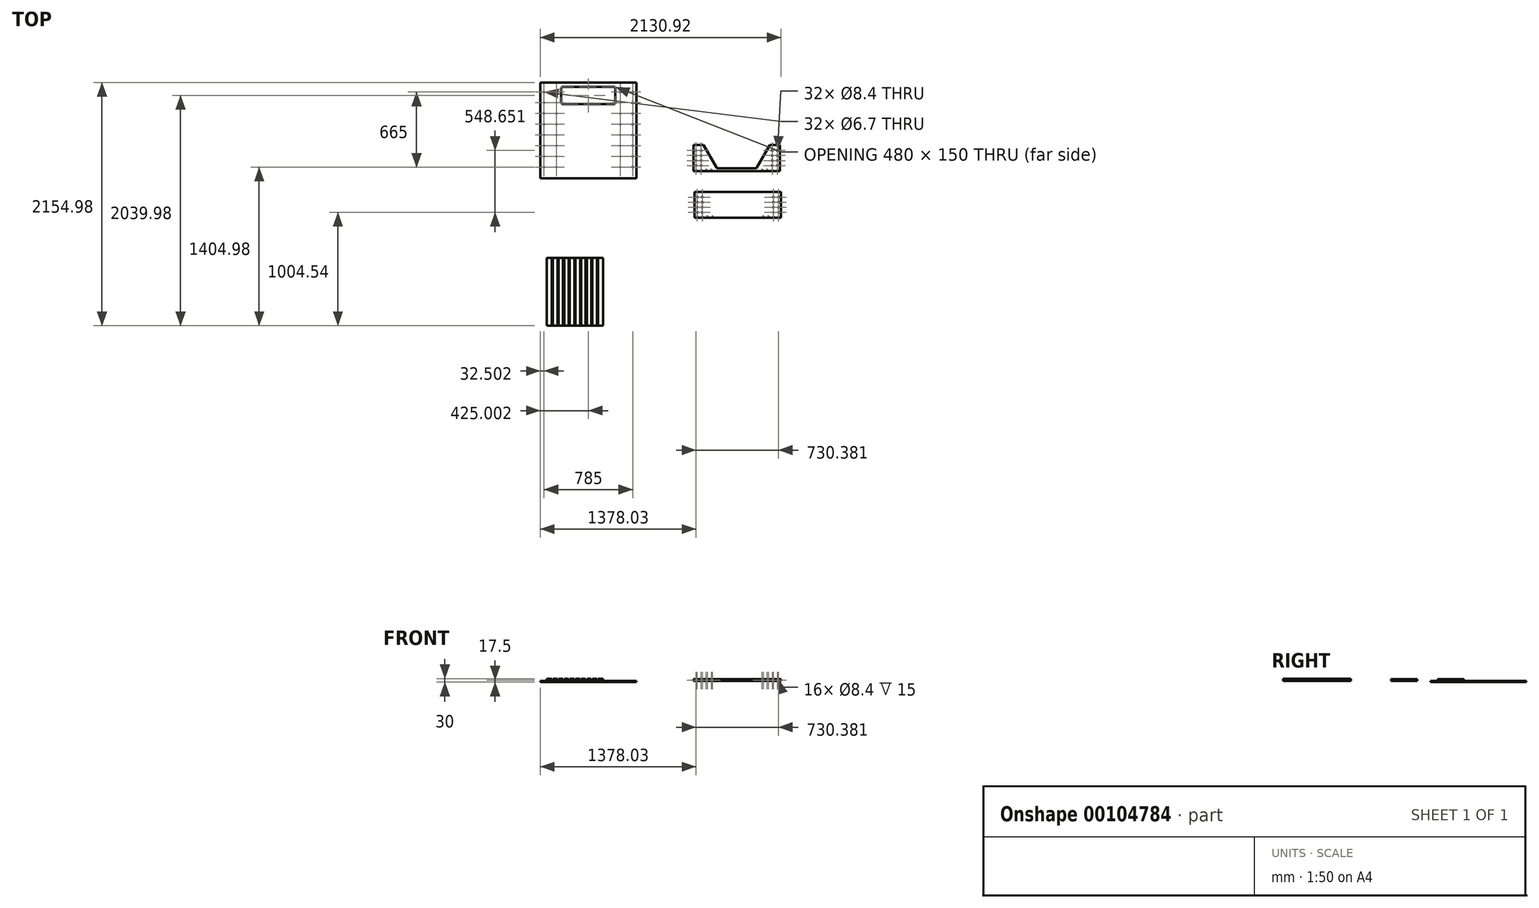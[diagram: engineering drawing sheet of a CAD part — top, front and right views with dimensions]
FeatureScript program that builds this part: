
annotation { "Feature Type Name" : "Feature", "Feature Type Description" : "" }
export const myFeature = defineFeature(function(context is Context, id is Id, definition is map)
    precondition{}
    {
        {
            var Q0;
            Q0=qCreatedBy(makeId("Top.planeOp"),FACE);
            var sketch = newSketch(context, id + "F0", { "sketchPlane" : qUnion([Q0])});
            skLineSegment(sketch, "E0", {"start": v(-189.52, -105.86) * mm, "end": v(-189.52, -335.86) * mm});
            skLineSegment(sketch, "E1", {"start": v(17.97, -309.36) * mm, "end": v(-99.52, -105.86) * mm});
            skLineSegment(sketch, "E2", {"start": v(-99.52, -105.86) * mm, "end": v(-189.52, -105.86) * mm});
            skLineSegment(sketch, "E3", {"start": v(575.48, -335.86) * mm, "end": v(575.48, -105.86) * mm});
            skLineSegment(sketch, "E4", {"start": v(575.48, -105.86) * mm, "end": v(485.48, -105.86) * mm});
            skLineSegment(sketch, "E5", {"start": v(485.48, -105.86) * mm, "end": v(368, -309.36) * mm});
            skLineSegment(sketch, "E6", {"start": v(365.4, -310.86) * mm, "end": v(20.57, -310.86) * mm});
            skLineSegment(sketch, "E7", {"start": v(-189.52, -335.86) * mm, "end": v(575.48, -335.86) * mm});
            skPoint(sketch, "E8.visualSharp", {"position": v(367.13, -310.86) * mm});
            skArc(sketch, "E8.filletArc", {"start": v(365.4, -310.86) * mm, "mid": v(366.9, -310.45) * mm, "end": v(368, -309.36) * mm});
            skPoint(sketch, "E9.visualSharp", {"position": v(18.84, -310.86) * mm});
            skArc(sketch, "E9.filletArc", {"start": v(17.97, -309.36) * mm, "mid": v(19.07, -310.45) * mm, "end": v(20.57, -310.86) * mm});
            skCircle(sketch, "E10", {"center": v(-167.02, -153.36) * mm, "radius": 4.2 * mm});
            skCircle(sketch, "E11", {"center": v(-122.02, -153.36) * mm, "radius": 4.2 * mm});
            skCircle(sketch, "E12", {"center": v(-167.02, -198.36) * mm, "radius": 4.2 * mm});
            skCircle(sketch, "E13", {"center": v(-122.02, -198.36) * mm, "radius": 4.2 * mm});
            skCircle(sketch, "E14", {"center": v(-167.02, -243.36) * mm, "radius": 4.2 * mm});
            skCircle(sketch, "E15", {"center": v(-122.02, -243.36) * mm, "radius": 4.2 * mm});
            skCircle(sketch, "E16", {"center": v(-167.02, -288.36) * mm, "radius": 4.2 * mm});
            skCircle(sketch, "E17", {"center": v(-122.02, -288.36) * mm, "radius": 4.2 * mm});
            skCircle(sketch, "E18", {"center": v(507.98, -153.36) * mm, "radius": 4.2 * mm});
            skCircle(sketch, "E19", {"center": v(552.98, -153.36) * mm, "radius": 4.2 * mm});
            skCircle(sketch, "E20", {"center": v(507.98, -198.36) * mm, "radius": 4.2 * mm});
            skCircle(sketch, "E21", {"center": v(552.98, -198.36) * mm, "radius": 4.2 * mm});
            skCircle(sketch, "E22", {"center": v(507.98, -243.36) * mm, "radius": 4.2 * mm});
            skCircle(sketch, "E23", {"center": v(552.98, -243.36) * mm, "radius": 4.2 * mm});
            skCircle(sketch, "E24", {"center": v(507.98, -288.36) * mm, "radius": 4.2 * mm});
            skCircle(sketch, "E25", {"center": v(552.98, -288.36) * mm, "radius": 4.2 * mm});
            skLineSegment(sketch, "E26.bottom", {"start": v(-179.13, -519.5) * mm, "end": v(585.87, -519.5) * mm});
            skLineSegment(sketch, "E26.top", {"start": v(-179.13, -749.5) * mm, "end": v(585.87, -749.5) * mm});
            skLineSegment(sketch, "E26.left", {"start": v(-179.13, -519.5) * mm, "end": v(-179.13, -749.5) * mm});
            skLineSegment(sketch, "E26.right", {"start": v(585.87, -519.5) * mm, "end": v(585.87, -749.5) * mm});
            skCircle(sketch, "E27", {"center": v(-156.63, -567) * mm, "radius": 4.2 * mm});
            skCircle(sketch, "E28", {"center": v(-111.63, -567) * mm, "radius": 4.2 * mm});
            skCircle(sketch, "E29", {"center": v(-156.63, -612) * mm, "radius": 4.2 * mm});
            skCircle(sketch, "E30", {"center": v(-111.63, -612) * mm, "radius": 4.2 * mm});
            skCircle(sketch, "E31", {"center": v(-156.63, -657) * mm, "radius": 4.2 * mm});
            skCircle(sketch, "E32", {"center": v(-111.63, -657) * mm, "radius": 4.2 * mm});
            skCircle(sketch, "E33", {"center": v(-156.63, -702) * mm, "radius": 4.2 * mm});
            skCircle(sketch, "E34", {"center": v(-111.63, -702) * mm, "radius": 4.2 * mm});
            skCircle(sketch, "E35", {"center": v(518.37, -567) * mm, "radius": 4.2 * mm});
            skCircle(sketch, "E36", {"center": v(563.37, -567) * mm, "radius": 4.2 * mm});
            skCircle(sketch, "E37", {"center": v(518.37, -612) * mm, "radius": 4.2 * mm});
            skCircle(sketch, "E38", {"center": v(563.37, -612) * mm, "radius": 4.2 * mm});
            skCircle(sketch, "E39", {"center": v(518.37, -657) * mm, "radius": 4.2 * mm});
            skCircle(sketch, "E40", {"center": v(563.37, -657) * mm, "radius": 4.2 * mm});
            skCircle(sketch, "E41", {"center": v(518.37, -702) * mm, "radius": 4.2 * mm});
            skCircle(sketch, "E42", {"center": v(563.37, -702) * mm, "radius": 4.2 * mm});
            skLineSegment(sketch, "E43.bottom", {"start": v(-1545.05, 448.43) * mm, "end": v(-695.05, 448.43) * mm});
            skLineSegment(sketch, "E43.top", {"start": v(-1545.05, -401.57) * mm, "end": v(-695.05, -401.57) * mm});
            skLineSegment(sketch, "E43.left", {"start": v(-1545.05, 448.43) * mm, "end": v(-1545.05, -401.57) * mm});
            skLineSegment(sketch, "E43.right", {"start": v(-695.05, 448.43) * mm, "end": v(-695.05, -401.57) * mm});
            skPoint(sketch, "E44", {"position": v(-1512.55, 363.43) * mm});
            skPoint(sketch, "E45", {"position": v(-1402.55, 363.43) * mm});
            skPoint(sketch, "E46", {"position": v(-837.55, 363.43) * mm});
            skPoint(sketch, "E47", {"position": v(-727.55, 363.43) * mm});
            skPoint(sketch, "E48", {"position": v(-1512.55, -301.57) * mm});
            skPoint(sketch, "E49", {"position": v(-1402.55, -301.57) * mm});
            skPoint(sketch, "E50", {"position": v(-837.55, -301.57) * mm});
            skPoint(sketch, "E51", {"position": v(-727.55, -301.57) * mm});
            skPoint(sketch, "E52", {"position": v(-1512.55, 268.43) * mm});
            skPoint(sketch, "E53", {"position": v(-1512.55, -16.57) * mm});
            skPoint(sketch, "E54", {"position": v(-1512.55, -206.57) * mm});
            skPoint(sketch, "E55", {"position": v(-1512.55, -111.57) * mm});
            skPoint(sketch, "E56", {"position": v(-1512.55, 78.43) * mm});
            skPoint(sketch, "E57", {"position": v(-1512.55, 173.43) * mm});
            skPoint(sketch, "E58", {"position": v(-1402.55, 268.43) * mm});
            skPoint(sketch, "E59", {"position": v(-1402.55, 173.43) * mm});
            skPoint(sketch, "E60", {"position": v(-1402.55, 78.43) * mm});
            skPoint(sketch, "E61", {"position": v(-1402.55, -16.57) * mm});
            skPoint(sketch, "E62", {"position": v(-1402.55, -111.57) * mm});
            skPoint(sketch, "E63", {"position": v(-1402.55, -206.57) * mm});
            skPoint(sketch, "E64", {"position": v(-837.55, 268.43) * mm});
            skPoint(sketch, "E65", {"position": v(-837.55, 173.43) * mm});
            skPoint(sketch, "E66", {"position": v(-837.55, 78.43) * mm});
            skPoint(sketch, "E67", {"position": v(-837.55, -16.57) * mm});
            skPoint(sketch, "E68", {"position": v(-837.55, -111.57) * mm});
            skPoint(sketch, "E69", {"position": v(-837.55, -206.57) * mm});
            skPoint(sketch, "E70", {"position": v(-727.55, 268.43) * mm});
            skPoint(sketch, "E71", {"position": v(-727.55, 173.43) * mm});
            skPoint(sketch, "E72", {"position": v(-727.55, 78.43) * mm});
            skPoint(sketch, "E73", {"position": v(-727.55, -16.57) * mm});
            skPoint(sketch, "E74", {"position": v(-727.55, -111.57) * mm});
            skPoint(sketch, "E75", {"position": v(-727.55, -206.57) * mm});
            skLineSegment(sketch, "E76.bottom", {"start": v(-1488.78, -1106.55) * mm, "end": v(-988.78, -1106.55) * mm});
            skLineSegment(sketch, "E76.top", {"start": v(-1488.78, -1706.55) * mm, "end": v(-988.78, -1706.55) * mm});
            skLineSegment(sketch, "E76.left", {"start": v(-1488.78, -1106.55) * mm, "end": v(-1488.78, -1706.55) * mm});
            skLineSegment(sketch, "E76.right", {"start": v(-988.78, -1106.55) * mm, "end": v(-988.78, -1706.55) * mm});
            skLineSegment(sketch, "E77.bottom", {"start": v(-1350.05, 408.43) * mm, "end": v(-890.05, 408.43) * mm});
            skLineSegment(sketch, "E77.top", {"start": v(-1350.05, 258.43) * mm, "end": v(-890.05, 258.43) * mm});
            skLineSegment(sketch, "E77.left", {"start": v(-1360.05, 398.43) * mm, "end": v(-1360.05, 268.43) * mm});
            skLineSegment(sketch, "E77.right", {"start": v(-880.05, 398.43) * mm, "end": v(-880.05, 268.43) * mm});
            skPoint(sketch, "E78.visualSharp", {"position": v(-1360.05, 408.43) * mm});
            skArc(sketch, "E78.filletArc", {"start": v(-1350.05, 408.43) * mm, "mid": v(-1357.12, 405.5) * mm, "end": v(-1360.05, 398.43) * mm});
            skPoint(sketch, "E79.visualSharp", {"position": v(-1360.05, 258.43) * mm});
            skArc(sketch, "E79.filletArc", {"start": v(-1360.05, 268.43) * mm, "mid": v(-1357.12, 261.36) * mm, "end": v(-1350.05, 258.43) * mm});
            skPoint(sketch, "E80.visualSharp", {"position": v(-880.05, 408.43) * mm});
            skArc(sketch, "E80.filletArc", {"start": v(-880.05, 398.43) * mm, "mid": v(-882.98, 405.5) * mm, "end": v(-890.05, 408.43) * mm});
            skPoint(sketch, "E81.visualSharp", {"position": v(-880.05, 258.43) * mm});
            skArc(sketch, "E81.filletArc", {"start": v(-890.05, 258.43) * mm, "mid": v(-882.98, 261.36) * mm, "end": v(-880.05, 268.43) * mm});
            skSolve(sketch);
        }
        {
            var Q0;
            Q0=makeQuery(id+"F0.imprint","IMPRINT",FACE,{"disambiguationData":[TD([[makeQuery(id+"F0.imprint","IMPRINT",EDGE,{"derivedFrom":sQuery(id+"F0.wireOp",EDGE,"E0")}),1.0]])]});
            extrude(context, id + "F1", {"entities" : qUnion([Q0]), "depth" : 15 * mm});
        }
        {
            var Q0;
            Q0=makeQuery(id+"F1.opExtrude","SWEPT_FACE",FACE,{"disambiguationData":[OSD([sQuery(id+"F0.wireOp",EDGE,"E7")])]});
            var sketch = newSketch(context, id + "F2", { "sketchPlane" : qUnion([Q0])});
            skCircle(sketch, "E82", {"center": v(-167.02, 7.5) * mm, "radius": 4.2 * mm});
            skCircle(sketch, "E83", {"center": v(-122.02, 7.5) * mm, "radius": 4.2 * mm});
            skCircle(sketch, "E84", {"center": v(-77.02, 7.5) * mm, "radius": 4.2 * mm});
            skCircle(sketch, "E85", {"center": v(-32.02, 7.5) * mm, "radius": 4.2 * mm});
            skCircle(sketch, "E86", {"center": v(552.98, 7.5) * mm, "radius": 4.2 * mm});
            skCircle(sketch, "E87", {"center": v(507.98, 7.5) * mm, "radius": 4.2 * mm});
            skCircle(sketch, "E88", {"center": v(462.98, 7.5) * mm, "radius": 4.2 * mm});
            skCircle(sketch, "E89", {"center": v(417.98, 7.5) * mm, "radius": 4.2 * mm});
            skPoint(sketch, "E90", {"position": v(-189.52, 7.5) * mm});
            skSolve(sketch);
        }
        {
            var Q0;
            Q0=makeQuery(id+"F2.imprint","IMPRINT",FACE,{"disambiguationData":[TD([[makeQuery(id+"F2.imprint","IMPRINT",EDGE,{"derivedFrom":sQuery(id+"F2.wireOp",EDGE,"E82")}),1.0]])]});
            var Q1;
            Q1=makeQuery(id+"F2.imprint","IMPRINT",FACE,{"disambiguationData":[TD([[makeQuery(id+"F2.imprint","IMPRINT",EDGE,{"derivedFrom":sQuery(id+"F2.wireOp",EDGE,"E83")}),1.0]])]});
            var Q2;
            Q2=makeQuery(id+"F2.imprint","IMPRINT",FACE,{"disambiguationData":[TD([[makeQuery(id+"F2.imprint","IMPRINT",EDGE,{"derivedFrom":sQuery(id+"F2.wireOp",EDGE,"E84")}),1.0]])]});
            var Q3;
            Q3=makeQuery(id+"F2.imprint","IMPRINT",FACE,{"disambiguationData":[TD([[makeQuery(id+"F2.imprint","IMPRINT",EDGE,{"derivedFrom":sQuery(id+"F2.wireOp",EDGE,"E85")}),1.0]])]});
            var Q4;
            Q4=makeQuery(id+"F2.imprint","IMPRINT",FACE,{"disambiguationData":[TD([[makeQuery(id+"F2.imprint","IMPRINT",EDGE,{"derivedFrom":sQuery(id+"F2.wireOp",EDGE,"E89")}),1.0]])]});
            var Q5;
            Q5=makeQuery(id+"F2.imprint","IMPRINT",FACE,{"disambiguationData":[TD([[makeQuery(id+"F2.imprint","IMPRINT",EDGE,{"derivedFrom":sQuery(id+"F2.wireOp",EDGE,"E88")}),1.0]])]});
            var Q6;
            Q6=makeQuery(id+"F2.imprint","IMPRINT",FACE,{"disambiguationData":[TD([[makeQuery(id+"F2.imprint","IMPRINT",EDGE,{"derivedFrom":sQuery(id+"F2.wireOp",EDGE,"E87")}),1.0]])]});
            var Q7;
            Q7=makeQuery(id+"F2.imprint","IMPRINT",FACE,{"disambiguationData":[TD([[makeQuery(id+"F2.imprint","IMPRINT",EDGE,{"derivedFrom":sQuery(id+"F2.wireOp",EDGE,"E86")}),1.0]])]});
            extrude(context, id + "F3", {"entities" : qUnion([Q0, Q1, Q2, Q3, Q4, Q5, Q6, Q7]), "operationType" : NewBodyOperationType.REMOVE, "oppositeDirection" : true, "depth" : 15 * mm});
        }
        {
            var Q0;
            Q0=makeQuery(id+"F0.imprint","IMPRINT",FACE,{"disambiguationData":[TD([[makeQuery(id+"F0.imprint","IMPRINT",EDGE,{"derivedFrom":sQuery(id+"F0.wireOp",EDGE,"E26.bottom")}),-1.0]])]});
            extrude(context, id + "F4", {"entities" : qUnion([Q0]), "depth" : 15 * mm});
        }
        {
            var Q0;
            Q0=makeQuery(id+"F4.opExtrude","SWEPT_FACE",FACE,{"disambiguationData":[OSD([sQuery(id+"F0.wireOp",EDGE,"E26.top")])]});
            var sketch = newSketch(context, id + "F5", { "sketchPlane" : qUnion([Q0])});
            skCircle(sketch, "E91", {"center": v(-156.63, 7.5) * mm, "radius": 4.2 * mm});
            skCircle(sketch, "E92", {"center": v(-111.63, 7.5) * mm, "radius": 4.2 * mm});
            skCircle(sketch, "E93", {"center": v(-66.63, 7.5) * mm, "radius": 4.2 * mm});
            skCircle(sketch, "E94", {"center": v(-21.63, 7.5) * mm, "radius": 4.2 * mm});
            skCircle(sketch, "E95", {"center": v(563.37, 7.5) * mm, "radius": 4.2 * mm});
            skCircle(sketch, "E96", {"center": v(518.37, 7.5) * mm, "radius": 4.2 * mm});
            skCircle(sketch, "E97", {"center": v(473.37, 7.5) * mm, "radius": 4.2 * mm});
            skCircle(sketch, "E98", {"center": v(428.37, 7.5) * mm, "radius": 4.2 * mm});
            skPoint(sketch, "E99", {"position": v(-179.13, 7.5) * mm});
            skSolve(sketch);
        }
        {
            var Q0;
            Q0=makeQuery(id+"F5.imprint","IMPRINT",FACE,{"disambiguationData":[TD([[makeQuery(id+"F5.imprint","IMPRINT",EDGE,{"derivedFrom":sQuery(id+"F5.wireOp",EDGE,"E91")}),1.0]])]});
            var Q1;
            Q1=makeQuery(id+"F5.imprint","IMPRINT",FACE,{"disambiguationData":[TD([[makeQuery(id+"F5.imprint","IMPRINT",EDGE,{"derivedFrom":sQuery(id+"F5.wireOp",EDGE,"E92")}),1.0]])]});
            var Q2;
            Q2=makeQuery(id+"F5.imprint","IMPRINT",FACE,{"disambiguationData":[TD([[makeQuery(id+"F5.imprint","IMPRINT",EDGE,{"derivedFrom":sQuery(id+"F5.wireOp",EDGE,"E93")}),1.0]])]});
            var Q3;
            Q3=makeQuery(id+"F5.imprint","IMPRINT",FACE,{"disambiguationData":[TD([[makeQuery(id+"F5.imprint","IMPRINT",EDGE,{"derivedFrom":sQuery(id+"F5.wireOp",EDGE,"E94")}),1.0]])]});
            var Q4;
            Q4=makeQuery(id+"F5.imprint","IMPRINT",FACE,{"disambiguationData":[TD([[makeQuery(id+"F5.imprint","IMPRINT",EDGE,{"derivedFrom":sQuery(id+"F5.wireOp",EDGE,"E98")}),1.0]])]});
            var Q5;
            Q5=makeQuery(id+"F5.imprint","IMPRINT",FACE,{"disambiguationData":[TD([[makeQuery(id+"F5.imprint","IMPRINT",EDGE,{"derivedFrom":sQuery(id+"F5.wireOp",EDGE,"E97")}),1.0]])]});
            var Q6;
            Q6=makeQuery(id+"F5.imprint","IMPRINT",FACE,{"disambiguationData":[TD([[makeQuery(id+"F5.imprint","IMPRINT",EDGE,{"derivedFrom":sQuery(id+"F5.wireOp",EDGE,"E96")}),1.0]])]});
            var Q7;
            Q7=makeQuery(id+"F5.imprint","IMPRINT",FACE,{"disambiguationData":[TD([[makeQuery(id+"F5.imprint","IMPRINT",EDGE,{"derivedFrom":sQuery(id+"F5.wireOp",EDGE,"E95")}),1.0]])]});
            extrude(context, id + "F6", {"entities" : qUnion([Q0, Q1, Q2, Q3, Q4, Q5, Q6, Q7]), "operationType" : NewBodyOperationType.REMOVE, "oppositeDirection" : true, "depth" : 15 * mm});
        }
        {
            var Q0;
            Q0=makeQuery(id+"F0.imprint","IMPRINT",FACE,{"disambiguationData":[TD([[makeQuery(id+"F0.imprint","IMPRINT",EDGE,{"derivedFrom":sQuery(id+"F0.wireOp",EDGE,"E43.bottom")}),-1.0]])]});
            extrude(context, id + "F7", {"entities" : qUnion([Q0]), "oppositeDirection" : true, "depth" : 10 * mm});
        }
        {
            var Q0;
            Q0=sQuery(id+"F0.wireOp",VERTEX,"E44");
            var Q1;
            Q1=sQuery(id+"F0.wireOp",VERTEX,"E52");
            var Q2;
            Q2=sQuery(id+"F0.wireOp",VERTEX,"E57");
            var Q3;
            Q3=sQuery(id+"F0.wireOp",VERTEX,"E56");
            var Q4;
            Q4=sQuery(id+"F0.wireOp",VERTEX,"E53");
            var Q5;
            Q5=sQuery(id+"F0.wireOp",VERTEX,"E55");
            var Q6;
            Q6=sQuery(id+"F0.wireOp",VERTEX,"E54");
            var Q7;
            Q7=sQuery(id+"F0.wireOp",VERTEX,"E48");
            var Q8;
            Q8=sQuery(id+"F0.wireOp",VERTEX,"E49");
            var Q9;
            Q9=sQuery(id+"F0.wireOp",VERTEX,"E63");
            var Q10;
            Q10=sQuery(id+"F0.wireOp",VERTEX,"E62");
            var Q11;
            Q11=sQuery(id+"F0.wireOp",VERTEX,"E61");
            var Q12;
            Q12=sQuery(id+"F0.wireOp",VERTEX,"E60");
            var Q13;
            Q13=sQuery(id+"F0.wireOp",VERTEX,"E59");
            var Q14;
            Q14=sQuery(id+"F0.wireOp",VERTEX,"E58");
            var Q15;
            Q15=sQuery(id+"F0.wireOp",VERTEX,"E45");
            var Q16;
            Q16=sQuery(id+"F0.wireOp",VERTEX,"E46");
            var Q17;
            Q17=sQuery(id+"F0.wireOp",VERTEX,"E64");
            var Q18;
            Q18=sQuery(id+"F0.wireOp",VERTEX,"E65");
            var Q19;
            Q19=sQuery(id+"F0.wireOp",VERTEX,"E66");
            var Q20;
            Q20=sQuery(id+"F0.wireOp",VERTEX,"E67");
            var Q21;
            Q21=sQuery(id+"F0.wireOp",VERTEX,"E68");
            var Q22;
            Q22=sQuery(id+"F0.wireOp",VERTEX,"E69");
            var Q23;
            Q23=sQuery(id+"F0.wireOp",VERTEX,"E50");
            var Q24;
            Q24=sQuery(id+"F0.wireOp",VERTEX,"E51");
            var Q25;
            Q25=sQuery(id+"F0.wireOp",VERTEX,"E75");
            var Q26;
            Q26=sQuery(id+"F0.wireOp",VERTEX,"E74");
            var Q27;
            Q27=sQuery(id+"F0.wireOp",VERTEX,"E73");
            var Q28;
            Q28=sQuery(id+"F0.wireOp",VERTEX,"E72");
            var Q29;
            Q29=sQuery(id+"F0.wireOp",VERTEX,"E71");
            var Q30;
            Q30=sQuery(id+"F0.wireOp",VERTEX,"E70");
            var Q31;
            Q31=sQuery(id+"F0.wireOp",VERTEX,"E47");
            var Q32;
            Q32=makeQuery(id+"F7.opExtrude","SWEPT_BODY",BODY,{"disambiguationData":[OSD([sQuery(id+"F0.wireOp",EDGE,"E43.bottom"),sQuery(id+"F0.wireOp",EDGE,"E43.top"),sQuery(id+"F0.wireOp",EDGE,"E43.left"),sQuery(id+"F0.wireOp",EDGE,"E43.right")])]});
            hole(context, id + "F8", {"style" : HoleStyle.SIMPLE, "endStyle" : HoleEndStyle.THROUGH, "holeDiameter" : 6.7 * mm, "isTappedThrough" : true, "tappedDepth" : 12 * mm, "tapClearance" : 3, "locations" : qUnion([Q0, Q1, Q2, Q3, Q4, Q5, Q6, Q7, Q8, Q9, Q10, Q11, Q12, Q13, Q14, Q15, Q16, Q17, Q18, Q19, Q20, Q21, Q22, Q23, Q24, Q25, Q26, Q27, Q28, Q29, Q30, Q31]), "scope" : qUnion([Q32])});
        }
        {
            var Q0;
            Q0=makeQuery(id+"F0.imprint","IMPRINT",FACE,{"disambiguationData":[TD([[makeQuery(id+"F0.imprint","IMPRINT",EDGE,{"derivedFrom":sQuery(id+"F0.wireOp",EDGE,"E76.bottom")}),-1.0]])]});
            extrude(context, id + "F9", {"entities" : qUnion([Q0]), "depth" : 20 * mm});
        }
        {
            var Q0;
            Q0=makeQuery(id+"F9.opExtrude","SWEPT_FACE",FACE,{"disambiguationData":[OSD([sQuery(id+"F0.wireOp",EDGE,"E76.top")])]});
            var sketch = newSketch(context, id + "F10", { "sketchPlane" : qUnion([Q0])});
            skLineSegment(sketch, "E100", {"start": v(-1443.78, 20) * mm, "end": v(-1443.78, 13.5) * mm});
            skLineSegment(sketch, "E101", {"start": v(-1443.78, 13.5) * mm, "end": v(-1446.78, 13.5) * mm});
            skLineSegment(sketch, "E102", {"start": v(-1446.78, 13.5) * mm, "end": v(-1446.78, 5.5) * mm});
            skLineSegment(sketch, "E103", {"start": v(-1446.78, 5.5) * mm, "end": v(-1430.78, 5.5) * mm});
            skLineSegment(sketch, "E104", {"start": v(-1430.78, 5.5) * mm, "end": v(-1430.78, 13.5) * mm});
            skLineSegment(sketch, "E105", {"start": v(-1430.78, 13.5) * mm, "end": v(-1433.78, 13.5) * mm});
            skLineSegment(sketch, "E106", {"start": v(-1433.78, 13.5) * mm, "end": v(-1433.78, 20) * mm});
            skLineSegment(sketch, "E107", {"start": v(-1433.78, 20) * mm, "end": v(-1443.78, 20) * mm});
            skLineSegment(sketch, "E108", {"start": v(-1393.78, 20) * mm, "end": v(-1393.78, 13.5) * mm});
            skLineSegment(sketch, "E109", {"start": v(-1393.78, 13.5) * mm, "end": v(-1396.78, 13.5) * mm});
            skLineSegment(sketch, "E110", {"start": v(-1396.78, 13.5) * mm, "end": v(-1396.78, 5.5) * mm});
            skLineSegment(sketch, "E111", {"start": v(-1396.78, 5.5) * mm, "end": v(-1380.78, 5.5) * mm});
            skLineSegment(sketch, "E112", {"start": v(-1380.78, 5.5) * mm, "end": v(-1380.78, 13.5) * mm});
            skLineSegment(sketch, "E113", {"start": v(-1380.78, 13.5) * mm, "end": v(-1383.78, 13.5) * mm});
            skLineSegment(sketch, "E114", {"start": v(-1383.78, 13.5) * mm, "end": v(-1383.78, 20) * mm});
            skLineSegment(sketch, "E115", {"start": v(-1383.78, 20) * mm, "end": v(-1393.78, 20) * mm});
            skLineSegment(sketch, "E116", {"start": v(-1343.78, 20) * mm, "end": v(-1343.78, 13.5) * mm});
            skLineSegment(sketch, "E117", {"start": v(-1343.78, 13.5) * mm, "end": v(-1346.78, 13.5) * mm});
            skLineSegment(sketch, "E118", {"start": v(-1346.78, 13.5) * mm, "end": v(-1346.78, 5.5) * mm});
            skLineSegment(sketch, "E119", {"start": v(-1346.78, 5.5) * mm, "end": v(-1330.78, 5.5) * mm});
            skLineSegment(sketch, "E120", {"start": v(-1330.78, 5.5) * mm, "end": v(-1330.78, 13.5) * mm});
            skLineSegment(sketch, "E121", {"start": v(-1330.78, 13.5) * mm, "end": v(-1333.78, 13.5) * mm});
            skLineSegment(sketch, "E122", {"start": v(-1333.78, 13.5) * mm, "end": v(-1333.78, 20) * mm});
            skLineSegment(sketch, "E123", {"start": v(-1333.78, 20) * mm, "end": v(-1343.78, 20) * mm});
            skLineSegment(sketch, "E124", {"start": v(-1293.78, 20) * mm, "end": v(-1293.78, 13.5) * mm});
            skLineSegment(sketch, "E125", {"start": v(-1293.78, 13.5) * mm, "end": v(-1296.78, 13.5) * mm});
            skLineSegment(sketch, "E126", {"start": v(-1296.78, 13.5) * mm, "end": v(-1296.78, 5.5) * mm});
            skLineSegment(sketch, "E127", {"start": v(-1296.78, 5.5) * mm, "end": v(-1280.78, 5.5) * mm});
            skLineSegment(sketch, "E128", {"start": v(-1280.78, 5.5) * mm, "end": v(-1280.78, 13.5) * mm});
            skLineSegment(sketch, "E129", {"start": v(-1280.78, 13.5) * mm, "end": v(-1283.78, 13.5) * mm});
            skLineSegment(sketch, "E130", {"start": v(-1283.78, 13.5) * mm, "end": v(-1283.78, 20) * mm});
            skLineSegment(sketch, "E131", {"start": v(-1283.78, 20) * mm, "end": v(-1293.78, 20) * mm});
            skLineSegment(sketch, "E132", {"start": v(-1243.78, 20) * mm, "end": v(-1243.78, 13.5) * mm});
            skLineSegment(sketch, "E133", {"start": v(-1243.78, 13.5) * mm, "end": v(-1246.78, 13.5) * mm});
            skLineSegment(sketch, "E134", {"start": v(-1246.78, 13.5) * mm, "end": v(-1246.78, 5.5) * mm});
            skLineSegment(sketch, "E135", {"start": v(-1246.78, 5.5) * mm, "end": v(-1230.78, 5.5) * mm});
            skLineSegment(sketch, "E136", {"start": v(-1230.78, 5.5) * mm, "end": v(-1230.78, 13.5) * mm});
            skLineSegment(sketch, "E137", {"start": v(-1230.78, 13.5) * mm, "end": v(-1233.78, 13.5) * mm});
            skLineSegment(sketch, "E138", {"start": v(-1233.78, 13.5) * mm, "end": v(-1233.78, 20) * mm});
            skLineSegment(sketch, "E139", {"start": v(-1233.78, 20) * mm, "end": v(-1243.78, 20) * mm});
            skLineSegment(sketch, "E140", {"start": v(-1193.78, 20) * mm, "end": v(-1193.78, 13.5) * mm});
            skLineSegment(sketch, "E141", {"start": v(-1193.78, 13.5) * mm, "end": v(-1196.78, 13.5) * mm});
            skLineSegment(sketch, "E142", {"start": v(-1196.78, 13.5) * mm, "end": v(-1196.78, 5.5) * mm});
            skLineSegment(sketch, "E143", {"start": v(-1196.78, 5.5) * mm, "end": v(-1180.78, 5.5) * mm});
            skLineSegment(sketch, "E144", {"start": v(-1180.78, 5.5) * mm, "end": v(-1180.78, 13.5) * mm});
            skLineSegment(sketch, "E145", {"start": v(-1180.78, 13.5) * mm, "end": v(-1183.78, 13.5) * mm});
            skLineSegment(sketch, "E146", {"start": v(-1183.78, 13.5) * mm, "end": v(-1183.78, 20) * mm});
            skLineSegment(sketch, "E147", {"start": v(-1183.78, 20) * mm, "end": v(-1193.78, 20) * mm});
            skLineSegment(sketch, "E148", {"start": v(-1143.78, 20) * mm, "end": v(-1143.78, 13.5) * mm});
            skLineSegment(sketch, "E149", {"start": v(-1143.78, 13.5) * mm, "end": v(-1146.78, 13.5) * mm});
            skLineSegment(sketch, "E150", {"start": v(-1146.78, 13.5) * mm, "end": v(-1146.78, 5.5) * mm});
            skLineSegment(sketch, "E151", {"start": v(-1146.78, 5.5) * mm, "end": v(-1130.78, 5.5) * mm});
            skLineSegment(sketch, "E152", {"start": v(-1130.78, 5.5) * mm, "end": v(-1130.78, 13.5) * mm});
            skLineSegment(sketch, "E153", {"start": v(-1130.78, 13.5) * mm, "end": v(-1133.78, 13.5) * mm});
            skLineSegment(sketch, "E154", {"start": v(-1133.78, 13.5) * mm, "end": v(-1133.78, 20) * mm});
            skLineSegment(sketch, "E155", {"start": v(-1133.78, 20) * mm, "end": v(-1143.78, 20) * mm});
            skLineSegment(sketch, "E156", {"start": v(-1093.78, 20) * mm, "end": v(-1093.78, 13.5) * mm});
            skLineSegment(sketch, "E157", {"start": v(-1093.78, 13.5) * mm, "end": v(-1096.78, 13.5) * mm});
            skLineSegment(sketch, "E158", {"start": v(-1096.78, 13.5) * mm, "end": v(-1096.78, 5.5) * mm});
            skLineSegment(sketch, "E159", {"start": v(-1096.78, 5.5) * mm, "end": v(-1080.78, 5.5) * mm});
            skLineSegment(sketch, "E160", {"start": v(-1080.78, 5.5) * mm, "end": v(-1080.78, 13.5) * mm});
            skLineSegment(sketch, "E161", {"start": v(-1080.78, 13.5) * mm, "end": v(-1083.78, 13.5) * mm});
            skLineSegment(sketch, "E162", {"start": v(-1083.78, 13.5) * mm, "end": v(-1083.78, 20) * mm});
            skLineSegment(sketch, "E163", {"start": v(-1083.78, 20) * mm, "end": v(-1093.78, 20) * mm});
            skLineSegment(sketch, "E164", {"start": v(-1043.78, 20) * mm, "end": v(-1043.78, 13.5) * mm});
            skLineSegment(sketch, "E165", {"start": v(-1043.78, 13.5) * mm, "end": v(-1046.78, 13.5) * mm});
            skLineSegment(sketch, "E166", {"start": v(-1046.78, 13.5) * mm, "end": v(-1046.78, 5.5) * mm});
            skLineSegment(sketch, "E167", {"start": v(-1046.78, 5.5) * mm, "end": v(-1030.78, 5.5) * mm});
            skLineSegment(sketch, "E168", {"start": v(-1030.78, 5.5) * mm, "end": v(-1030.78, 13.5) * mm});
            skLineSegment(sketch, "E169", {"start": v(-1030.78, 13.5) * mm, "end": v(-1033.78, 13.5) * mm});
            skLineSegment(sketch, "E170", {"start": v(-1033.78, 13.5) * mm, "end": v(-1033.78, 20) * mm});
            skLineSegment(sketch, "E171", {"start": v(-1033.78, 20) * mm, "end": v(-1043.78, 20) * mm});
            skSolve(sketch);
        }
        {
            var Q0;
            Q0=makeQuery(id+"F10.imprint","IMPRINT",FACE,{"disambiguationData":[TD([[makeQuery(id+"F10.imprint","IMPRINT",EDGE,{"derivedFrom":sQuery(id+"F10.wireOp",EDGE,"E164")}),1.0]])]});
            var Q1;
            Q1=makeQuery(id+"F10.imprint","IMPRINT",FACE,{"disambiguationData":[TD([[makeQuery(id+"F10.imprint","IMPRINT",EDGE,{"derivedFrom":sQuery(id+"F10.wireOp",EDGE,"E156")}),1.0]])]});
            var Q2;
            Q2=makeQuery(id+"F10.imprint","IMPRINT",FACE,{"disambiguationData":[TD([[makeQuery(id+"F10.imprint","IMPRINT",EDGE,{"derivedFrom":sQuery(id+"F10.wireOp",EDGE,"E148")}),1.0]])]});
            var Q3;
            Q3=makeQuery(id+"F10.imprint","IMPRINT",FACE,{"disambiguationData":[TD([[makeQuery(id+"F10.imprint","IMPRINT",EDGE,{"derivedFrom":sQuery(id+"F10.wireOp",EDGE,"E140")}),1.0]])]});
            var Q4;
            Q4=makeQuery(id+"F10.imprint","IMPRINT",FACE,{"disambiguationData":[TD([[makeQuery(id+"F10.imprint","IMPRINT",EDGE,{"derivedFrom":sQuery(id+"F10.wireOp",EDGE,"E132")}),1.0]])]});
            var Q5;
            Q5=makeQuery(id+"F10.imprint","IMPRINT",FACE,{"disambiguationData":[TD([[makeQuery(id+"F10.imprint","IMPRINT",EDGE,{"derivedFrom":sQuery(id+"F10.wireOp",EDGE,"E124")}),1.0]])]});
            var Q6;
            Q6=makeQuery(id+"F10.imprint","IMPRINT",FACE,{"disambiguationData":[TD([[makeQuery(id+"F10.imprint","IMPRINT",EDGE,{"derivedFrom":sQuery(id+"F10.wireOp",EDGE,"E116")}),1.0]])]});
            var Q7;
            Q7=makeQuery(id+"F10.imprint","IMPRINT",FACE,{"disambiguationData":[TD([[makeQuery(id+"F10.imprint","IMPRINT",EDGE,{"derivedFrom":sQuery(id+"F10.wireOp",EDGE,"E108")}),1.0]])]});
            var Q8;
            Q8=makeQuery(id+"F10.imprint","IMPRINT",FACE,{"disambiguationData":[TD([[makeQuery(id+"F10.imprint","IMPRINT",EDGE,{"derivedFrom":sQuery(id+"F10.wireOp",EDGE,"E100")}),1.0]])]});
            extrude(context, id + "F11", {"entities" : qUnion([Q0, Q1, Q2, Q3, Q4, Q5, Q6, Q7, Q8]), "operationType" : NewBodyOperationType.REMOVE, "oppositeDirection" : true, "depth" : 600 * mm});
        }
    });
